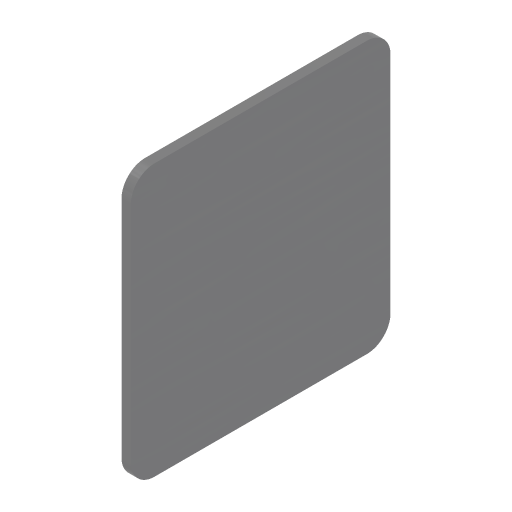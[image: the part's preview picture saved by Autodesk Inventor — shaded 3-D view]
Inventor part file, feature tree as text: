
AUTODESK INVENTOR PART (.ipt)
format: ipt  version: 2024.1 (Build 281209000, 209)  size: 177,152 bytes
history: native  units: mm
features: extrude x1, sketch x1
ambient origin geometry x8: Origin, YZ Plane, XZ Plane, XY Plane, X Axis, Y Axis, Z Axis, Center Point
bodies: Solid1 (feature_tree)
feature tree (2):
  extrude  "Extrusion1"  Depth=230.0mm
  sketch  "Sketch1"  dims[d0=220.0mm d1=230.0mm d2=20.0mm d3=8.0mm d4=0.0mm]
